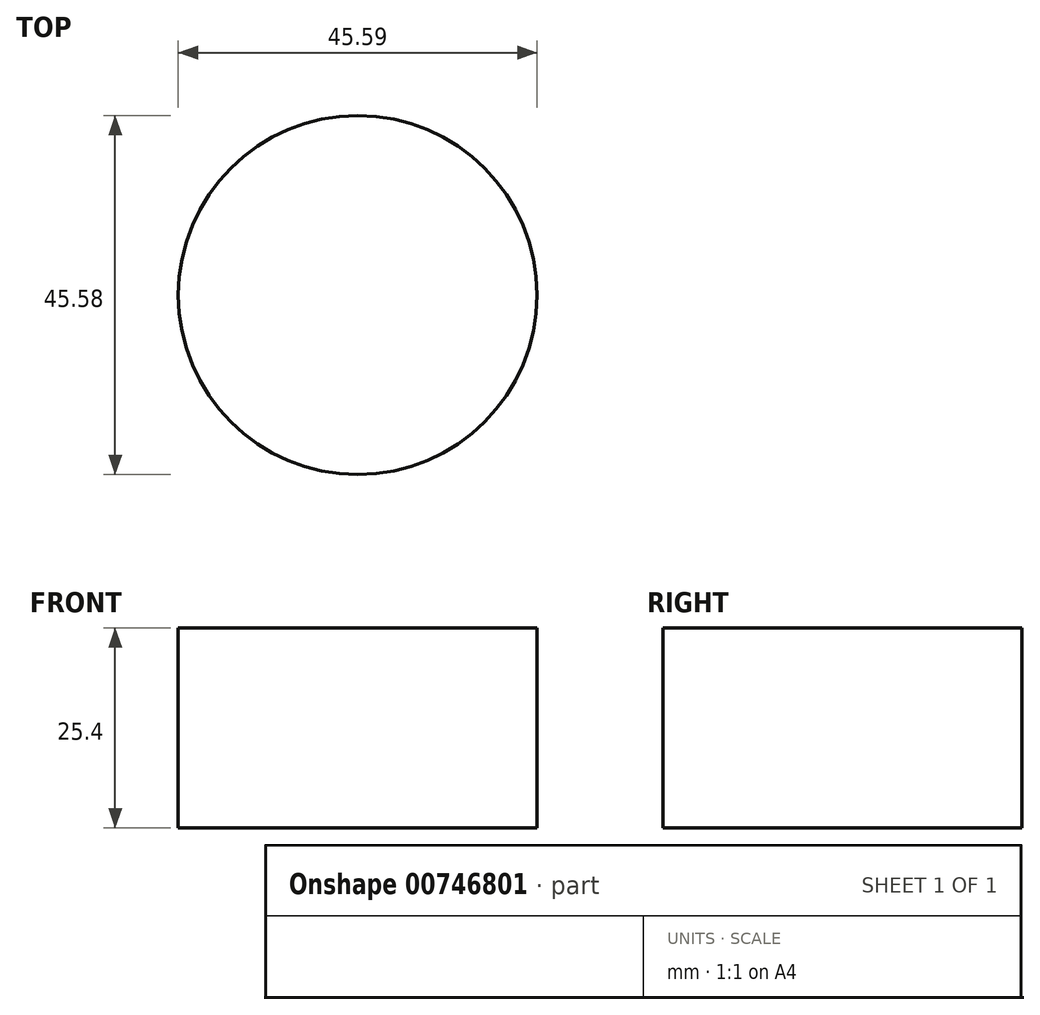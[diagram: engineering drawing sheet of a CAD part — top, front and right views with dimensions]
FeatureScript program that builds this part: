
annotation { "Feature Type Name" : "Feature", "Feature Type Description" : "" }
export const myFeature = defineFeature(function(context is Context, id is Id, definition is map)
    precondition{}
    {
        {
            var Q0;
            Q0=qCreatedBy(makeId("Top.planeOp"),FACE);
            var sketch = newSketch(context, id + "F0", { "sketchPlane" : qUnion([Q0])});
            skCircle(sketch, "E0", {"center": v(-27.03, 24.89) * mm, "radius": 22.8 * mm});
            skArc(sketch, "E1", {"start": v(-42.5, 8.15) * mm, "mid": v(-28.89, 24.43) * mm, "end": v(-48.46, 32.64) * mm});
            skSolve(sketch);
        }
        {
            var Q0;
            Q0 = qSketchRegion(id + "F0", true);
            extrude(context, id + "F1", {"entities" : qUnion([Q0]), "depth" : 25.4 * mm, "offsetDistance" : 25.4 * mm});
        }
    });
